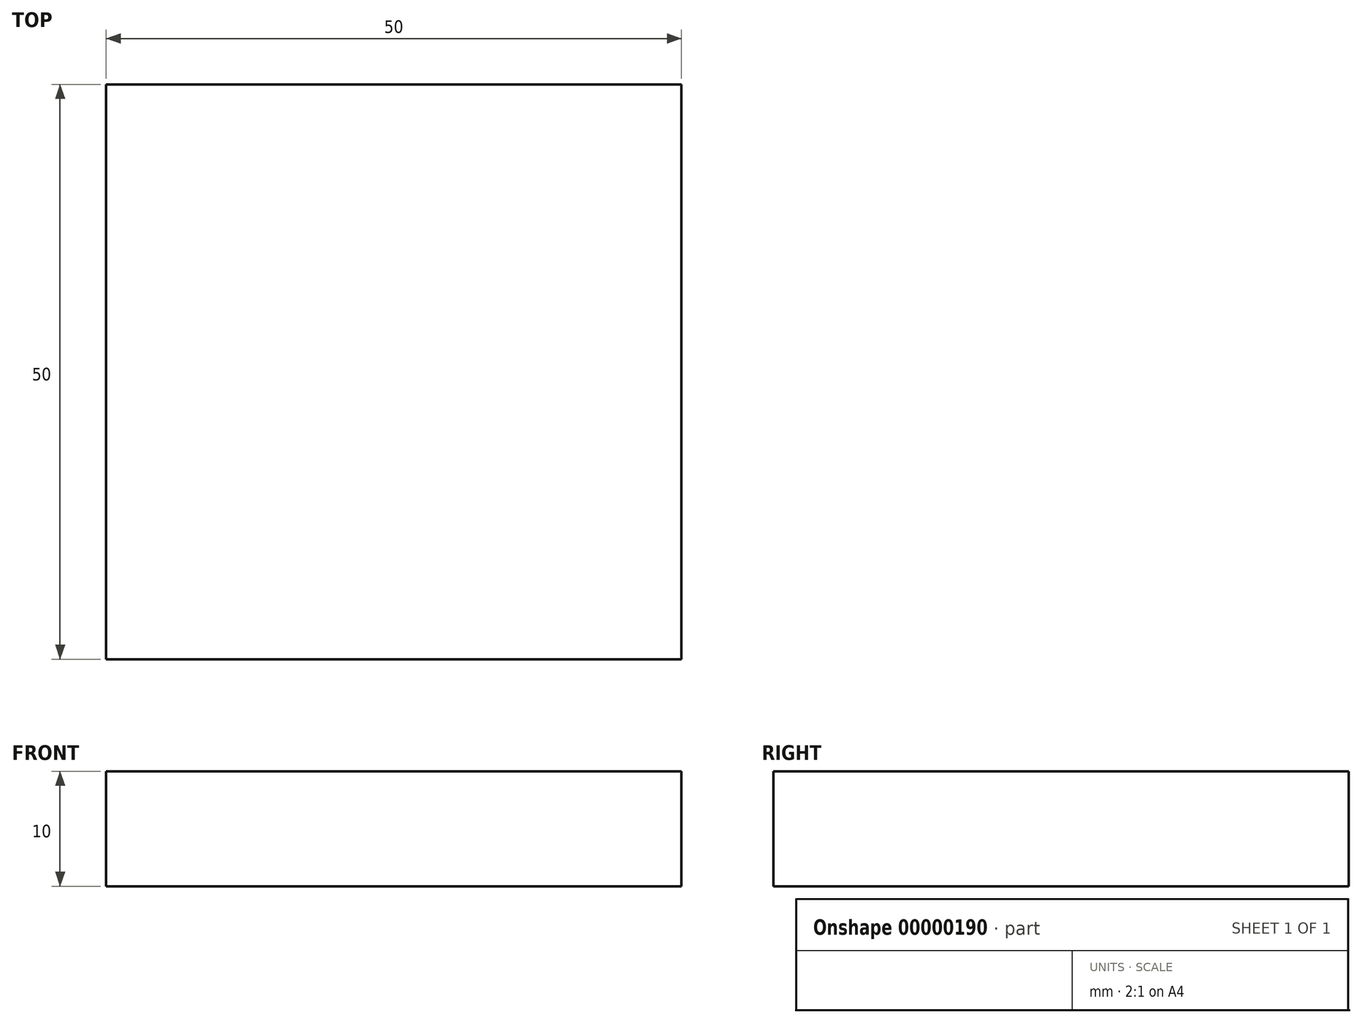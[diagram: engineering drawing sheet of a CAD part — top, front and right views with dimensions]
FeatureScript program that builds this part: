
annotation { "Feature Type Name" : "Feature", "Feature Type Description" : "" }
export const myFeature = defineFeature(function(context is Context, id is Id, definition is map)
    precondition{}
    {
        {
            var Q0;
            Q0=qCreatedBy(makeId("Top.planeOp"),FACE);
            var sketch = newSketch(context, id + "F0", { "sketchPlane" : qUnion([Q0])});
            skLineSegment(sketch, "E0.rect.bottom", {"start": v(-25, 25) * mm, "end": v(25, 25) * mm});
            skLineSegment(sketch, "E0.rect.top", {"start": v(-25, -25) * mm, "end": v(25, -25) * mm});
            skLineSegment(sketch, "E0.rect.left", {"start": v(-25, 25) * mm, "end": v(-25, -25) * mm});
            skLineSegment(sketch, "E0.rect.right", {"start": v(25, 25) * mm, "end": v(25, -25) * mm});
            skPoint(sketch, "E0.rect.middle", {"position": v(0, 0) * mm});
            skSolve(sketch);
        }
        {
            var Q0;
            Q0=makeQuery(id+"F0.imprint","IMPRINT",FACE,{"disambiguationData":[TD([[makeQuery(id+"F0.imprint","IMPRINT",EDGE,{"derivedFrom":sQuery(id+"F0.wireOp",EDGE,"E0.rect.bottom")}),-1.0]])]});
            extrude(context, id + "F1", {"entities" : qUnion([Q0]), "depth" : 10 * mm});
        }
    });
